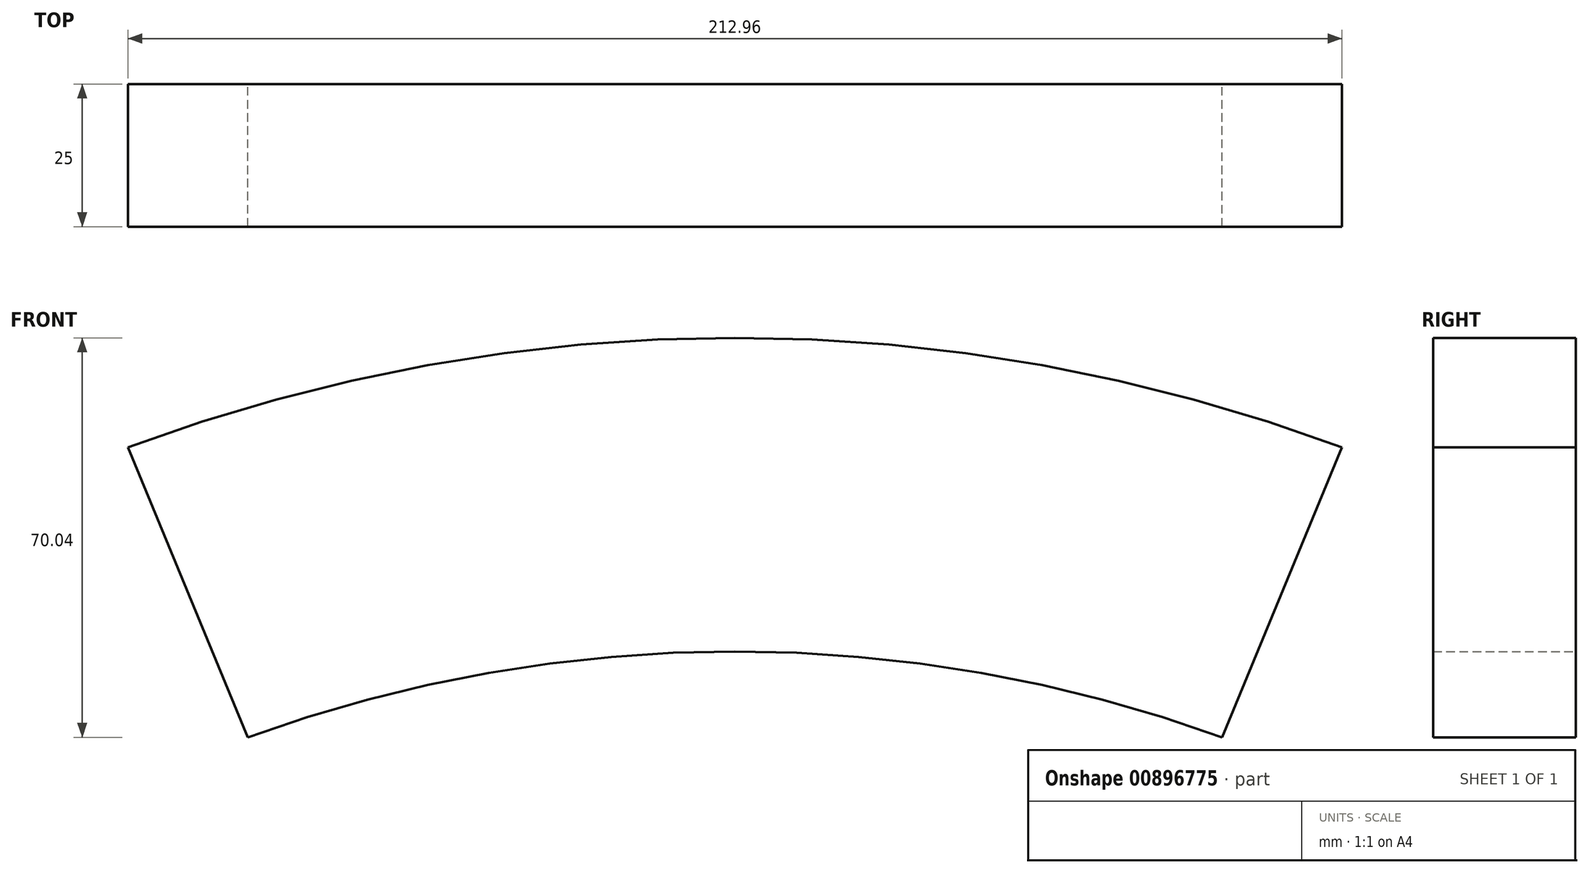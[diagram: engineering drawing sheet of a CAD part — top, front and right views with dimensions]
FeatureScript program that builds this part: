
annotation { "Feature Type Name" : "Feature", "Feature Type Description" : "" }
export const myFeature = defineFeature(function(context is Context, id is Id, definition is map)
    precondition{}
    {
        {
            var Q0;
            Q0=qCreatedBy(makeId("Front.planeOp"),FACE);
            var sketch = newSketch(context, id + "F0", { "sketchPlane" : qUnion([Q0])});
            skCircle(sketch, "E0", {"center": v(0, 0) * mm, "radius": 305 * mm});
            skCircle(sketch, "E1", {"center": v(0, 0) * mm, "radius": 250 * mm});
            skLineSegment(sketch, "E2", {"start": v(0, 0) * mm, "end": v(0, 28.74) * mm});
            skLineSegment(sketch, "E3", {"start": v(0, 28.74) * mm, "end": v(106.48, 285.8) * mm});
            skLineSegment(sketch, "E4", {"start": v(0, 0) * mm, "end": v(20.33, 20.33) * mm});
            skLineSegment(sketch, "E5", {"start": v(20.33, 20.33) * mm, "end": v(126.8, 277.4) * mm});
            skLineSegment(sketch, "E6", {"start": v(0, 28.74) * mm, "end": v(-106.48, 285.8) * mm});
            skSolve(sketch);
        }
        {
            var Q0;
            {var subQ0=sQuery(id+"F0.wireOp",EDGE,"E3");var subQ1=sQuery(id+"F0.wireOp",EDGE,"E0");var subQ2=makeQuery(id+"F0.imprint","INTERSECT",VERTEX,{"derivedFrom":[subQ1,subQ0]});Q0=makeQuery(id+"F0.imprint","IMPRINT",FACE,{"disambiguationData":[TD([[makeQuery(id+"F0.imprint","IMPRINT",EDGE,{"disambiguationData":[TD([[subQ2,-1.0]])],"derivedFrom":subQ1}),1.0]])]});}
            extrude(context, id + "F1", {"entities" : qUnion([Q0]), "depth" : 25 * mm, "offsetDistance" : 25 * mm});
        }
    });
